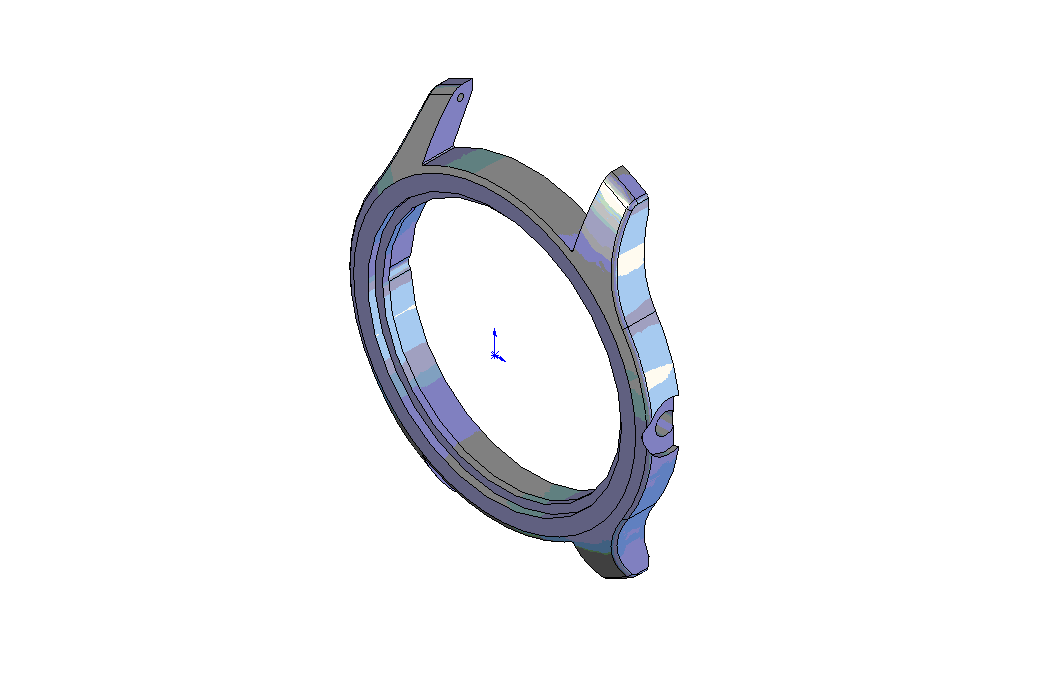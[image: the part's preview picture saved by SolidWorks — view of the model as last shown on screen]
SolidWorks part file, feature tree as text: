
SOLIDWORKS PART (.sldprt)
format: sldprt  version: not decoded by parser v0  size: 384,512 bytes
history: native  units: mm
features: sketch x11, cut_extrude x8, fillet x3, cut_revolve x2, mirror x2, material x1, extrude x1, plane x1 (+15 scaffold rows collapsed)
feature tree (44):
  scaffold x15  (default folders/planes/origin — collapsed)
  material  "Chrome Stainless Steel"
  sketch  "Sketch1"  dims[c1.D1=36.25mm c1.D2=45.9mm c1.D3=35.1mm c1.D5=36.25mm c1.D6=36.25mm c1.D4=18.1mm c2.D6=20.0mm]
  extrude  "Extrude1"  Depth=6.35mm
  sketch  "Sketch2"  dims[D1=28.702mm]
  cut_extrude  "Cut-Extrude1"  [1 undecoded]
  sketch  "Sketch3"  dims[D1=30.5308mm]
  cut_extrude  "Cut-Extrude2"  Depth=0.8636mm
  sketch  "Sketch4"  dims[c1.D2=20.0mm c1.D4=20.0mm c1.D1=25.4mm c2.D2=~17.393322mm c2.D3=33.909mm c2.D4=18.0mm]
  cut_revolve  "Cut-Revolve1"  Angle=360deg
  sketch  "Sketch5"  dims[c1.D1=5.0292mm c1.D2=34.544mm c1.D3=~1.669317mm c2.D3=45.0deg c2.D4=0.889mm c2.D5=43.561mm c2.D6=~8.474375mm c3.D6=30.0deg]
  cut_revolve  "Cut-Revolve2"  Angle=360deg
  sketch  "Sketch6"  dims[D1=2.4892mm D2=1.8796mm]
  cut_extrude  "Cut-Extrude3"  [1 undecoded]
  plane  "Plane1"
  sketch  "Sketch7"  dims[D1=5.7912mm]
  cut_extrude  "Cut-Extrude4"  Depth=0.7112mm
  sketch  "Sketch8"  dims[D1=32.2326mm]
  cut_extrude  "Cut-Extrude5"  Depth=0.4064mm
  fillet  "Fillet1"  Radius=1.524mm
  fillet  "Fillet2"  Radius=0.508mm
  fillet  "Fillet3"  Radius=0.1016mm
  sketch  "Sketch9"  dims[D1=29.464mm]
  cut_extrude  "Cut-Extrude6"  Depth=3.4036mm
  sketch  "Sketch10"  dims[c1.D1=~1.152478mm c1.D2=2.032mm c2.D1=3.1242mm]
  cut_extrude  "Cut-Extrude7"  [1 undecoded]
  sketch  "Sketch11"  dims[D1=0.762mm D2=1.397mm D3=1.27mm]
  cut_extrude  "Cut-Extrude8"  Depth=0.762mm
  mirror  "Mirror1"
  mirror  "Mirror2"
decode coverage: 22 of 27 modeling features carry decoded parameters
note: ~ marks probable driven/reference dimensions
note: 3 parameter values undecoded
summary: no parameter record found for 3 features
note: suppression state not decoded; provenance and decode notes live in map.json
